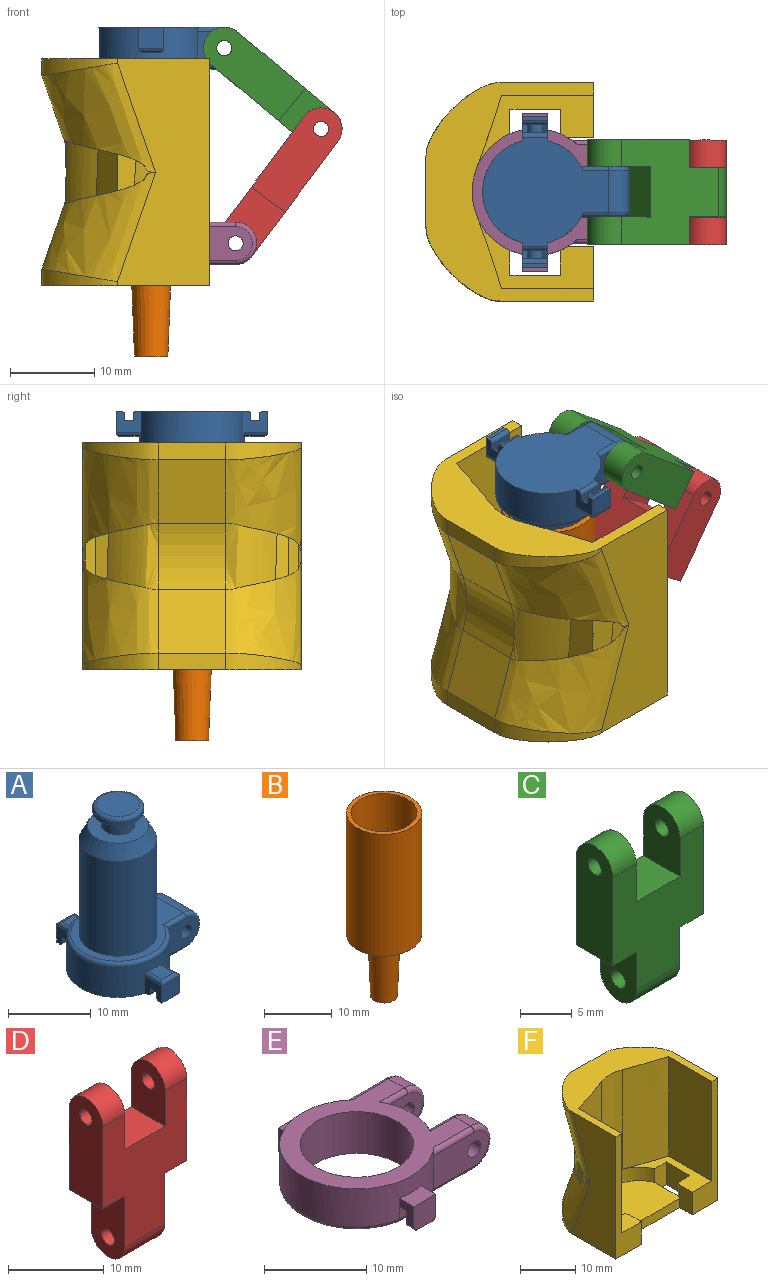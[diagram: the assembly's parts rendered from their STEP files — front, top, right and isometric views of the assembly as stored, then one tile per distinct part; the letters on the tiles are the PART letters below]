
ASSEMBLY  parts=6 mates=6
PART A: 52 faces, bbox 18.2x18x24.4 mm
  f0: cylinder r=2mm len=4mm, axis (0,0,-1), area 27mm2, adj f8,f31
  f1: plane 14.95x13mm, normal (0,0,-1), area 137.7mm2, adj f3,f4,f6,f7,f9,f14,f35,f37
  f2: plane 3x0.5mm, normal (0,0,-1), area 1.5mm2, adj f3,f4,f16,f36
  f3: plane 2.93x2.5mm, normal (-1,0,0), area 6.1mm2, adj f1,f2,f9,f16,f26,f27,f28,f35
  f4: plane 2.93x2.5mm, normal (1,0,0), area 6.1mm2, adj f1,f2,f9,f16,f26,f27,f29,f35
  f5: plane 3x0.5mm, normal (0,0,-1), area 1.5mm2, adj f6,f7,f19,f38
  f6: plane 2.93x2.5mm, normal (1,0,0), area 6.1mm2, adj f1,f5,f9,f19,f21,f22,f24,f37
  f7: plane 2.93x2.5mm, normal (-1,0,0), area 6.1mm2, adj f1,f5,f9,f19,f21,f22,f23,f37
  f8: plane 7.4x7.4mm, normal (0,0,1), area 30.4mm2, adj f0,f34
  f9: cylinder r=6.25mm len=12.5mm, axis (0,0,1), area 130.7mm2, adj f1,f3,f4,f6,f7,f12,f13,f17
  f10: plane 14.45x11.5mm, normal (0,0,1), area 50.2mm2, adj f11,f14,f47,f48,f49
  f11: cylinder r=4.7mm len=14mm, axis (0,0,1), area 413.4mm2, adj f10,f34
  f12: plane 5.22x4mm, normal (0,-1,0), area 16.6mm2, adj f9,f15,f45,f46,f47
  f13: plane 5.22x4mm, normal (0,1,0), area 16.6mm2, adj f9,f15,f49,f50,f51
  f14: cylinder r=2.5mm len=5mm, axis (0,1,0), area 39.3mm2, adj f1,f10,f46,f50
  f15: cylinder r=0.9mm len=6mm, axis (0,-1,0), area 33.9mm2, adj f12,f13
  f16: plane 3x2.5mm, normal (0,-1,0), area 7.5mm2, adj f2,f3,f4,f43
  f17: plane 2.33x2mm, normal (0,0,1), area 4.6mm2, adj f9,f42,f43,f44
  f18: plane 2.33x2mm, normal (0,0,1), area 4.6mm2, adj f9,f39,f40,f41
  f19: plane 3x2.5mm, normal (0,1,0), area 7.5mm2, adj f5,f6,f7,f40
  f20: cylinder r=1mm len=1.73mm, axis (0,-1,0), area 2.1mm2, adj f21,f22,f23,f24
  f21: plane 3x1mm, normal (0,1,0), area 2.2mm2, adj f6,f7,f20,f23,f24,f37
  f22: plane 3x1mm, normal (0,-1,0), area 2.2mm2, adj f6,f7,f20,f23,f24,f38
  f23: plane 1x0.63mm, normal (0.5,0,-0.87), area 0.7mm2, adj f7,f20,f21,f22
  f24: plane 1x0.63mm, normal (-0.5,0,-0.87), area 0.7mm2, adj f6,f20,f21,f22
  f25: cylinder r=1mm len=1.73mm, axis (0,1,0), area 2.1mm2, adj f26,f27,f28,f29
  f26: plane 3x1mm, normal (0,-1,0), area 2.2mm2, adj f3,f4,f25,f28,f29,f35
  f27: plane 3x1mm, normal (0,1,0), area 2.2mm2, adj f3,f4,f25,f28,f29,f36
  f28: plane 1x0.63mm, normal (0.5,0,-0.87), area 0.7mm2, adj f3,f25,f26,f27
  f29: plane 1x0.63mm, normal (-0.5,0,-0.87), area 0.7mm2, adj f4,f25,f26,f27
  f30: cylinder r=3.1mm len=6.2mm, axis (0,0,-1), area 9.7mm2, adj f31,f33
  f31: plane 6.2x6.2mm, normal (0,0,-1), area 17.6mm2, adj f0,f30
  f32: plane 5.2x5.2mm, normal (0,0,1), area 21.2mm2, adj f33
  f33: torus R=2.6mm, axis (0,0,1), area 14.4mm2, adj f30,f32
  f34: cone r=3.7mm half-angle=26.6deg, axis (0,0,-1), area 59mm2, adj f8,f11
  f35: cylinder r=0.5mm len=3mm, axis (-1,0,0), area 2.4mm2, adj f1,f3,f4,f26
  f36: cylinder r=0.5mm len=3mm, axis (1,0,0), area 2.4mm2, adj f2,f3,f4,f27
  f37: cylinder r=0.5mm len=3mm, axis (1,0,0), area 2.4mm2, adj f1,f6,f7,f21
  f38: cylinder r=0.5mm len=3mm, axis (-1,0,0), area 2.4mm2, adj f5,f6,f7,f22
  f39: cylinder r=0.5mm len=2.93mm, axis (0,1,0), area 2.1mm2, adj f6,f9,f18,f40
  f40: cylinder r=0.5mm len=3mm, axis (-1,0,0), area 2.1mm2, adj f18,f19,f39,f41
  f41: cylinder r=0.5mm len=2.93mm, axis (0,1,0), area 2.1mm2, adj f7,f9,f18,f40
  f42: cylinder r=0.5mm len=2.93mm, axis (0,1,0), area 2.1mm2, adj f4,f9,f17,f43
  f43: cylinder r=0.5mm len=3mm, axis (1,0,0), area 2.1mm2, adj f16,f17,f42,f44
  f44: cylinder r=0.5mm len=2.93mm, axis (0,1,0), area 2.1mm2, adj f3,f9,f17,f43
  f45: cylinder r=0.5mm len=3.22mm, axis (-1,0,0), area 2.5mm2, adj f1,f9,f12,f46
  f46: torus R=2mm, axis (0,-1,0), area 5.7mm2, adj f12,f14,f45,f47
  f47: cylinder r=0.5mm len=3.52mm, axis (1,0,0), area 2.6mm2, adj f10,f12,f46,f48
  f48: torus R=5.75mm, axis (0,0,1), area 25.3mm2, adj f9,f10,f47,f49
  f49: cylinder r=0.5mm len=3.52mm, axis (-1,0,0), area 2.6mm2, adj f10,f13,f48,f50
  f50: torus R=2mm, axis (0,-1,0), area 5.7mm2, adj f13,f14,f49,f51
  f51: cylinder r=0.5mm len=3.22mm, axis (1,0,0), area 2.5mm2, adj f1,f9,f13,f50
PART B: 10 faces, bbox 11.1x11.1x33 mm
  f0: cone r=1.95mm half-angle=2.2deg, axis (0,0,1), area 115mm2, adj f1,f9
  f1: plane 3.96x3.96mm, normal (0,0,-1), area 4.8mm2, adj f0,f2
  f2: cone r=1.98mm half-angle=2.2deg, axis (0,0,1), area 121.8mm2, adj f1,f3
  f3: plane 5.4x5.4mm, normal (0,0,-1), area 5.9mm2, adj f2,f4
  f4: cylinder r=2.7mm len=5.4mm, axis (0,0,1), area 17mm2, adj f3,f5
  f5: cone r=2.7mm half-angle=70.7deg, axis (0,0,1), area 78.3mm2, adj f4,f6
  f6: cylinder r=5.55mm len=22mm, axis (0,0,1), area 767.2mm2, adj f5,f7
  f7: plane 11.1x11.1mm, normal (0,0,1), area 22.1mm2, adj f6,f8
  f8: cylinder r=4.88mm len=21.52mm, axis (0,0,1), area 659.2mm2, adj f7,f9
  f9: cone r=4.88mm half-angle=70.7deg, axis (0,0,1), area 66.5mm2, adj f0,f8
PART C: 17 faces, bbox 12.5x5x20 mm
  f0: plane 6x5mm, normal (0,0,1), area 30mm2, adj f4,f5,f6,f14
  f1: plane 7x5mm, normal (1,0,0), area 29.5mm2, adj f2,f5,f6,f8,f10
  f2: plane 5x3.28mm, normal (0,0,-1), area 16.4mm2, adj f1,f3,f5,f6
  f3: plane 13x5mm, normal (1,0,0), area 59.8mm2, adj f2,f5,f6,f7,f9
  f4: plane 7x5mm, normal (-1,0,0), area 29.8mm2, adj f0,f5,f6,f7,f9
  f5: plane 15x12.45mm, normal (0,-1,0), area 130.3mm2, adj f0,f1,f2,f3,f4,f7,f8,f11
  f6: plane 15x12.45mm, normal (0,1,0), area 130.3mm2, adj f0,f1,f2,f3,f4,f7,f8,f11
  f7: cylinder r=2.5mm len=5mm, axis (1,0,0), area 25.3mm2, adj f3,f4,f5,f6
  f8: cylinder r=2.5mm len=5.9mm, axis (-1,0,0), area 46.3mm2, adj f1,f5,f6,f11
  f9: cylinder r=0.9mm len=3.23mm, axis (1,0,0), area 18.2mm2, adj f3,f4
  f10: cylinder r=0.95mm len=5.9mm, axis (1,0,0), area 35.2mm2, adj f1,f11
  f11: plane 7x5mm, normal (-1,0,0), area 29.5mm2, adj f5,f6,f8,f10,f12
  f12: plane 5x3.28mm, normal (0,0,-1), area 16.4mm2, adj f5,f6,f11,f13
  f13: plane 13x5mm, normal (-1,0,0), area 59.8mm2, adj f5,f6,f12,f15,f16
  f14: plane 7x5mm, normal (1,0,0), area 29.8mm2, adj f0,f5,f6,f15,f16
  f15: cylinder r=2.5mm len=5mm, axis (-1,0,0), area 25.3mm2, adj f5,f6,f13,f14
  f16: cylinder r=0.9mm len=3.23mm, axis (-1,0,0), area 18.2mm2, adj f13,f14
PART D: 17 faces, bbox 12.5x5x22 mm
  f0: plane 6x5mm, normal (0,0,1), area 30mm2, adj f4,f5,f6,f14
  f1: plane 9x5mm, normal (1,0,0), area 39.5mm2, adj f2,f5,f6,f8,f10
  f2: plane 5x3.28mm, normal (0,0,-1), area 16.4mm2, adj f1,f3,f5,f6
  f3: plane 13x5mm, normal (1,0,0), area 59.8mm2, adj f2,f5,f6,f7,f9
  f4: plane 7x5mm, normal (-1,0,0), area 29.8mm2, adj f0,f5,f6,f7,f9
  f5: plane 17x12.45mm, normal (0,-1,0), area 142.1mm2, adj f0,f1,f2,f3,f4,f7,f8,f11
  f6: plane 17x12.45mm, normal (0,1,0), area 142.1mm2, adj f0,f1,f2,f3,f4,f7,f8,f11
  f7: cylinder r=2.5mm len=5mm, axis (1,0,0), area 25.3mm2, adj f3,f4,f5,f6
  f8: cylinder r=2.5mm len=5.9mm, axis (-1,0,0), area 46.3mm2, adj f1,f5,f6,f11
  f9: cylinder r=0.9mm len=3.23mm, axis (1,0,0), area 18.2mm2, adj f3,f4
  f10: cylinder r=0.95mm len=5.9mm, axis (1,0,0), area 35.2mm2, adj f1,f11
  f11: plane 9x5mm, normal (-1,0,0), area 39.5mm2, adj f5,f6,f8,f10,f12
  f12: plane 5x3.28mm, normal (0,0,-1), area 16.4mm2, adj f5,f6,f11,f13
  f13: plane 13x5mm, normal (-1,0,0), area 59.8mm2, adj f5,f6,f12,f15,f16
  f14: plane 7x5mm, normal (1,0,0), area 29.8mm2, adj f0,f5,f6,f15,f16
  f15: cylinder r=2.5mm len=5mm, axis (-1,0,0), area 25.3mm2, adj f5,f6,f13,f14
  f16: cylinder r=0.9mm len=3.23mm, axis (-1,0,0), area 18.2mm2, adj f13,f14
PART E: 55 faces, bbox 20.9x18.8x5.4 mm
  f0: plane 17.1x13.8mm, normal (0,0,-1), area 79.2mm2, adj f4,f11,f12,f35,f36,f37,f42,f43
  f1: cylinder r=7.55mm len=15.1mm, axis (0,0,-1), area 133.9mm2, adj f5,f7,f9,f15,f16,f18,f20,f24
  f2: plane 2x1mm, normal (0,0,-1), area 2mm2, adj f25,f30,f51,f52
  f3: cylinder r=7.55mm len=7mm, axis (0,0,-1), area 27.9mm2, adj f5,f8,f10,f33,f36,f39
  f4: cylinder r=5.55mm len=11.1mm, axis (0,0,-1), area 174.4mm2, adj f0,f5
  f5: plane 17.6x15.1mm, normal (0,0,1), area 99.9mm2, adj f1,f3,f4,f11,f12,f33,f39,f40
  f6: plane 2x1mm, normal (0,0,-1), area 2mm2, adj f17,f21,f53,f54
  f7: plane 7.67x4mm, normal (0,-1,0), area 26.4mm2, adj f1,f14,f48,f49,f50
  f8: plane 5.12x4mm, normal (0,1,0), area 16.2mm2, adj f3,f14,f33,f34,f35
  f9: plane 7.67x4mm, normal (0,1,0), area 26.4mm2, adj f1,f13,f40,f41,f42
  f10: plane 5.12x4mm, normal (0,-1,0), area 16.2mm2, adj f3,f13,f37,f38,f39
  f11: cylinder r=2.5mm len=5mm, axis (0,-1,0), area 16.9mm2, adj f0,f5,f34,f49
  f12: cylinder r=2.5mm len=5mm, axis (0,-1,0), area 16.9mm2, adj f0,f5,f38,f41
  f13: cylinder r=0.9mm len=3.15mm, axis (0,-1,0), area 17.8mm2, adj f9,f10
  f14: cylinder r=0.9mm len=3.15mm, axis (0,-1,0), area 17.8mm2, adj f7,f8
  f15: plane 2.5x2mm, normal (-1,0,0), area 3.5mm2, adj f1,f17,f18,f19,f21,f54
  f16: plane 2.5x2mm, normal (1,0,0), area 3.5mm2, adj f1,f17,f18,f21,f22,f53
  f17: plane 3x3mm, normal (0,-1,0), area 8.9mm2, adj f6,f15,f16,f18,f53,f54
  f18: plane 3x2mm, normal (0,0,1), area 5.7mm2, adj f1,f15,f16,f17
  f19: plane 1x0.5mm, normal (0,0,-1), area 0.5mm2, adj f15,f20,f21,f23
  f20: plane 3x1.5mm, normal (0,-1,0), area 2.9mm2, adj f1,f19,f22,f23,f46
  f21: plane 3x2mm, normal (0,1,0), area 4.3mm2, adj f6,f15,f16,f19,f22,f23,f53,f54
  f22: plane 1x0.5mm, normal (0,0,-1), area 0.5mm2, adj f16,f20,f21,f23
  f23: cylinder r=1mm len=2mm, axis (0,-1,0), area 3.1mm2, adj f19,f20,f21,f22
  f24: plane 2.5x2mm, normal (-1,0,0), area 3.5mm2, adj f1,f25,f27,f30,f31,f52
  f25: plane 3x3mm, normal (0,1,0), area 8.9mm2, adj f2,f24,f26,f27,f51,f52
  f26: plane 2.5x2mm, normal (1,0,0), area 3.5mm2, adj f1,f25,f27,f30,f32,f51
  f27: plane 3x2mm, normal (0,0,1), area 5.7mm2, adj f1,f24,f25,f26
  f28: plane 3x1.5mm, normal (0,1,0), area 2.9mm2, adj f1,f29,f31,f32,f44
  f29: cylinder r=1mm len=2mm, axis (0,1,0), area 3.1mm2, adj f28,f30,f31,f32
  f30: plane 3x2mm, normal (0,-1,0), area 4.3mm2, adj f2,f24,f26,f29,f31,f32,f51,f52
  f31: plane 1x0.5mm, normal (0,0,-1), area 0.5mm2, adj f24,f28,f29,f30
  f32: plane 1x0.5mm, normal (0,0,-1), area 0.5mm2, adj f26,f28,f29,f30
  f33: cylinder r=0.5mm len=3.36mm, axis (-1,0,0), area 2.5mm2, adj f3,f5,f8,f34
  f34: torus R=2mm, axis (0,1,0), area 5.7mm2, adj f8,f11,f33,f35
  f35: cylinder r=0.5mm len=3.93mm, axis (1,0,0), area 2.7mm2, adj f0,f8,f34,f36
  f36: torus R=7.05mm, axis (0,0,1), area 5.2mm2, adj f0,f3,f35,f37
  f37: cylinder r=0.5mm len=3.93mm, axis (-1,0,0), area 2.7mm2, adj f0,f10,f36,f38
  f38: torus R=2mm, axis (0,1,0), area 5.7mm2, adj f10,f12,f37,f39
  f39: cylinder r=0.5mm len=3.36mm, axis (1,0,0), area 2.5mm2, adj f3,f5,f10,f38
  f40: cylinder r=0.5mm len=5.67mm, axis (-1,0,0), area 4.3mm2, adj f1,f5,f9,f41
  f41: torus R=2mm, axis (0,-1,0), area 5.7mm2, adj f9,f12,f40,f42
  f42: cylinder r=0.5mm len=5.83mm, axis (1,0,0), area 4.5mm2, adj f0,f9,f41,f43
  f43: torus R=7.05mm, axis (0,0,1), area 2.5mm2, adj f0,f1,f42,f44
  f44: cylinder r=0.5mm len=3mm, axis (1,0,0), area 2.3mm2, adj f0,f28,f43,f45
  f45: torus R=7.05mm, axis (0,0,1), area 15.8mm2, adj f0,f1,f44,f46
  f46: cylinder r=0.5mm len=3mm, axis (-1,0,0), area 2.3mm2, adj f0,f20,f45,f47
  f47: torus R=7.05mm, axis (0,0,1), area 2.5mm2, adj f0,f1,f46,f48
  f48: cylinder r=0.5mm len=5.83mm, axis (-1,0,0), area 4.5mm2, adj f0,f7,f47,f49
  f49: torus R=2mm, axis (0,-1,0), area 5.7mm2, adj f7,f11,f48,f50
  f50: cylinder r=0.5mm len=5.67mm, axis (1,0,0), area 4.3mm2, adj f1,f5,f7,f49
  f51: cylinder r=0.5mm len=1mm, axis (0,1,0), area 0.8mm2, adj f2,f25,f26,f30
  f52: cylinder r=0.5mm len=1mm, axis (0,-1,0), area 0.8mm2, adj f2,f24,f25,f30
  f53: cylinder r=0.5mm len=1mm, axis (0,1,0), area 0.8mm2, adj f6,f16,f17,f21
  f54: cylinder r=0.5mm len=1mm, axis (0,-1,0), area 0.8mm2, adj f6,f15,f17,f21
PART F: 42 faces, bbox 26x20.3x30.4 mm
  f0: cylinder r=7.5mm len=3mm, axis (0,0,1), area 2.5mm2, adj f1,f3,f33,f39
  f1: plane 14.03x8.88mm, normal (0,0,1), area 40.6mm2, adj f0,f2,f6,f28,f29,f33,f39,f40
  f2: cylinder r=7.5mm len=25mm, axis (0,0,1), area 169.8mm2, adj f1,f3,f5,f12,f29,f30,f35,f41
  f3: plane 13.75x11.24mm, normal (0,0,1), area 137mm2, adj f0,f2,f7,f31,f34,f38
  f4: plane 26x20mm, normal (0,0,-1), area 395.9mm2, adj f6,f9,f11,f13,f14,f20,f24,f31
  f5: plane 14.03x8.88mm, normal (0,0,1), area 40.6mm2, adj f2,f7,f9,f27,f30,f32,f35,f36
  f6: plane 27x6.5mm, normal (0,-1,0), area 65.5mm2, adj f1,f4,f11,f12,f28,f33
  f7: cylinder r=7.5mm len=3mm, axis (0,0,1), area 2.5mm2, adj f3,f5,f32,f37
  f8: bspline ~11.51x10.9mm, area 74.2mm2, adj f22,f23,f26,f28,f29
  f9: plane 27x6.5mm, normal (0,-1,0), area 65.5mm2, adj f4,f5,f12,f13,f27,f32
  f10: plane 8x2mm, normal (0,1,0), area 16mm2, adj f12,f15,f17,f21
  f11: plane 27x11mm, normal (1,0,0), area 238mm2, adj f4,f6,f12,f21,f22,f23,f24
  f12: plane 26x20mm, normal (0,0,1), area 177.6mm2, adj f2,f6,f9,f10,f11,f13,f17,f21
  f13: plane 27x11mm, normal (-1,0,0), area 238mm2, adj f4,f9,f12,f17,f18,f19,f20
  f14: plane 8x2mm, normal (0,1,0), area 16mm2, adj f4,f16,f20,f24
  f15: plane 8x7.56mm, normal (0,0.94,-0.33), area 64mm2, adj f10,f18,f22,f26
  f16: plane 8x7.56mm, normal (0,0.94,0.33), area 64mm2, adj f14,f19,f23,f26
  f17: bspline ~9x9mm, area 19.1mm2, adj f10,f12,f13,f18
  f18: bspline ~18.7x13.98mm, area 148.4mm2, adj f13,f15,f17,f25
  f19: bspline ~18.7x13.98mm, area 148.4mm2, adj f13,f16,f20,f25
  f20: bspline ~9x9mm, area 19.1mm2, adj f4,f13,f14,f19
  f21: bspline ~9x9mm, area 19.1mm2, adj f10,f11,f12,f22
  f22: bspline ~18.7x13.98mm, area 148.4mm2, adj f8,f11,f15,f21
  f23: bspline ~18.7x13.98mm, area 148.4mm2, adj f8,f11,f16,f24
  f24: bspline ~9x9mm, area 19.1mm2, adj f4,f11,f14,f23
  f25: bspline ~11.5x10.9mm, area 74.2mm2, adj f18,f19,f26,f27,f30
  f26: cylinder r=12mm len=8mm, axis (-1,0,0), area 64.3mm2, adj f8,f15,f16,f25
  f27: plane 22.03x11.03mm, normal (1,0,0), area 242mm2, adj f5,f9,f12,f25,f30
  f28: plane 22.03x11.03mm, normal (-1,0,0), area 242mm2, adj f1,f6,f8,f12,f29
  f29: cylinder r=169mm len=22mm, axis (0,0,-1), area 206.5mm2, adj f1,f2,f8,f12,f28
  f30: cylinder r=169mm len=22mm, axis (0,0,1), area 206.5mm2, adj f2,f5,f12,f25,f27
  f31: plane 13x2mm, normal (0,-1,0), area 26mm2, adj f3,f4,f32,f33
  f32: plane 5x3.26mm, normal (1,0,0), area 16.3mm2, adj f4,f5,f7,f9,f31
  f33: plane 5x3.26mm, normal (-1,0,0), area 16.3mm2, adj f0,f1,f4,f6,f31
  f34: plane 6x2mm, normal (-1,0,0), area 12mm2, adj f3,f4,f35,f37
  f35: plane 5x3mm, normal (0,-1,0), area 15mm2, adj f2,f4,f5,f34,f36
  f36: plane 6x5mm, normal (1,0,0), area 30mm2, adj f4,f5,f35,f37
  f37: plane 5x3mm, normal (0,1,0), area 15mm2, adj f4,f5,f7,f34,f36
  f38: plane 6x2mm, normal (1,0,0), area 12mm2, adj f3,f4,f39,f41
  f39: plane 5x3mm, normal (0,1,0), area 15mm2, adj f0,f1,f4,f38,f40
  f40: plane 6x5mm, normal (-1,0,0), area 30mm2, adj f1,f4,f39,f41
  f41: plane 5x3mm, normal (0,-1,0), area 15mm2, adj f1,f2,f4,f38,f40
PLACE A rot(axis=(1,0,0),180deg) t=(0.18,0.05,12.16)mm
PLACE B t=(0.18,0.05,-0.08)mm fixed
PLACE C rot(axis=(0.39,-0.39,-0.83),100.4deg) t=(17.32,0.05,13.11)mm
PLACE D rot(axis=(0.3,0.3,0.91),95.7deg) t=(13.22,0,0.93)mm
PLACE E t=(0.18,0.05,-3.08)mm
PLACE F rot(axis=(0,0,1),90deg) t=(-2.82,0.05,5.37)mm
MATE revolute D.f8 <-> E.f11  axis (0,-1,0) through (10.23,-2.95,-3.08)mm
MATE cylindrical F.f0 <-> E.f1  axis (0,0,1) through (0.18,0.05,6.37)mm
MATE revolute C.f10 <-> D.f7  axis (0,-1,0) through (20.39,3,10.55)mm
MATE cylindrical A.f9 <-> B.f0  axis (0,0,-1) through (0.18,0.05,10.66)mm
MATE fastened E.f4 <-> B.f0  axis (0,0,-1) through (0.18,0.05,-5.58)mm
MATE revolute C.f15 <-> A.f14  axis (0,1,0) through (8.88,-2.95,20.16)mm
